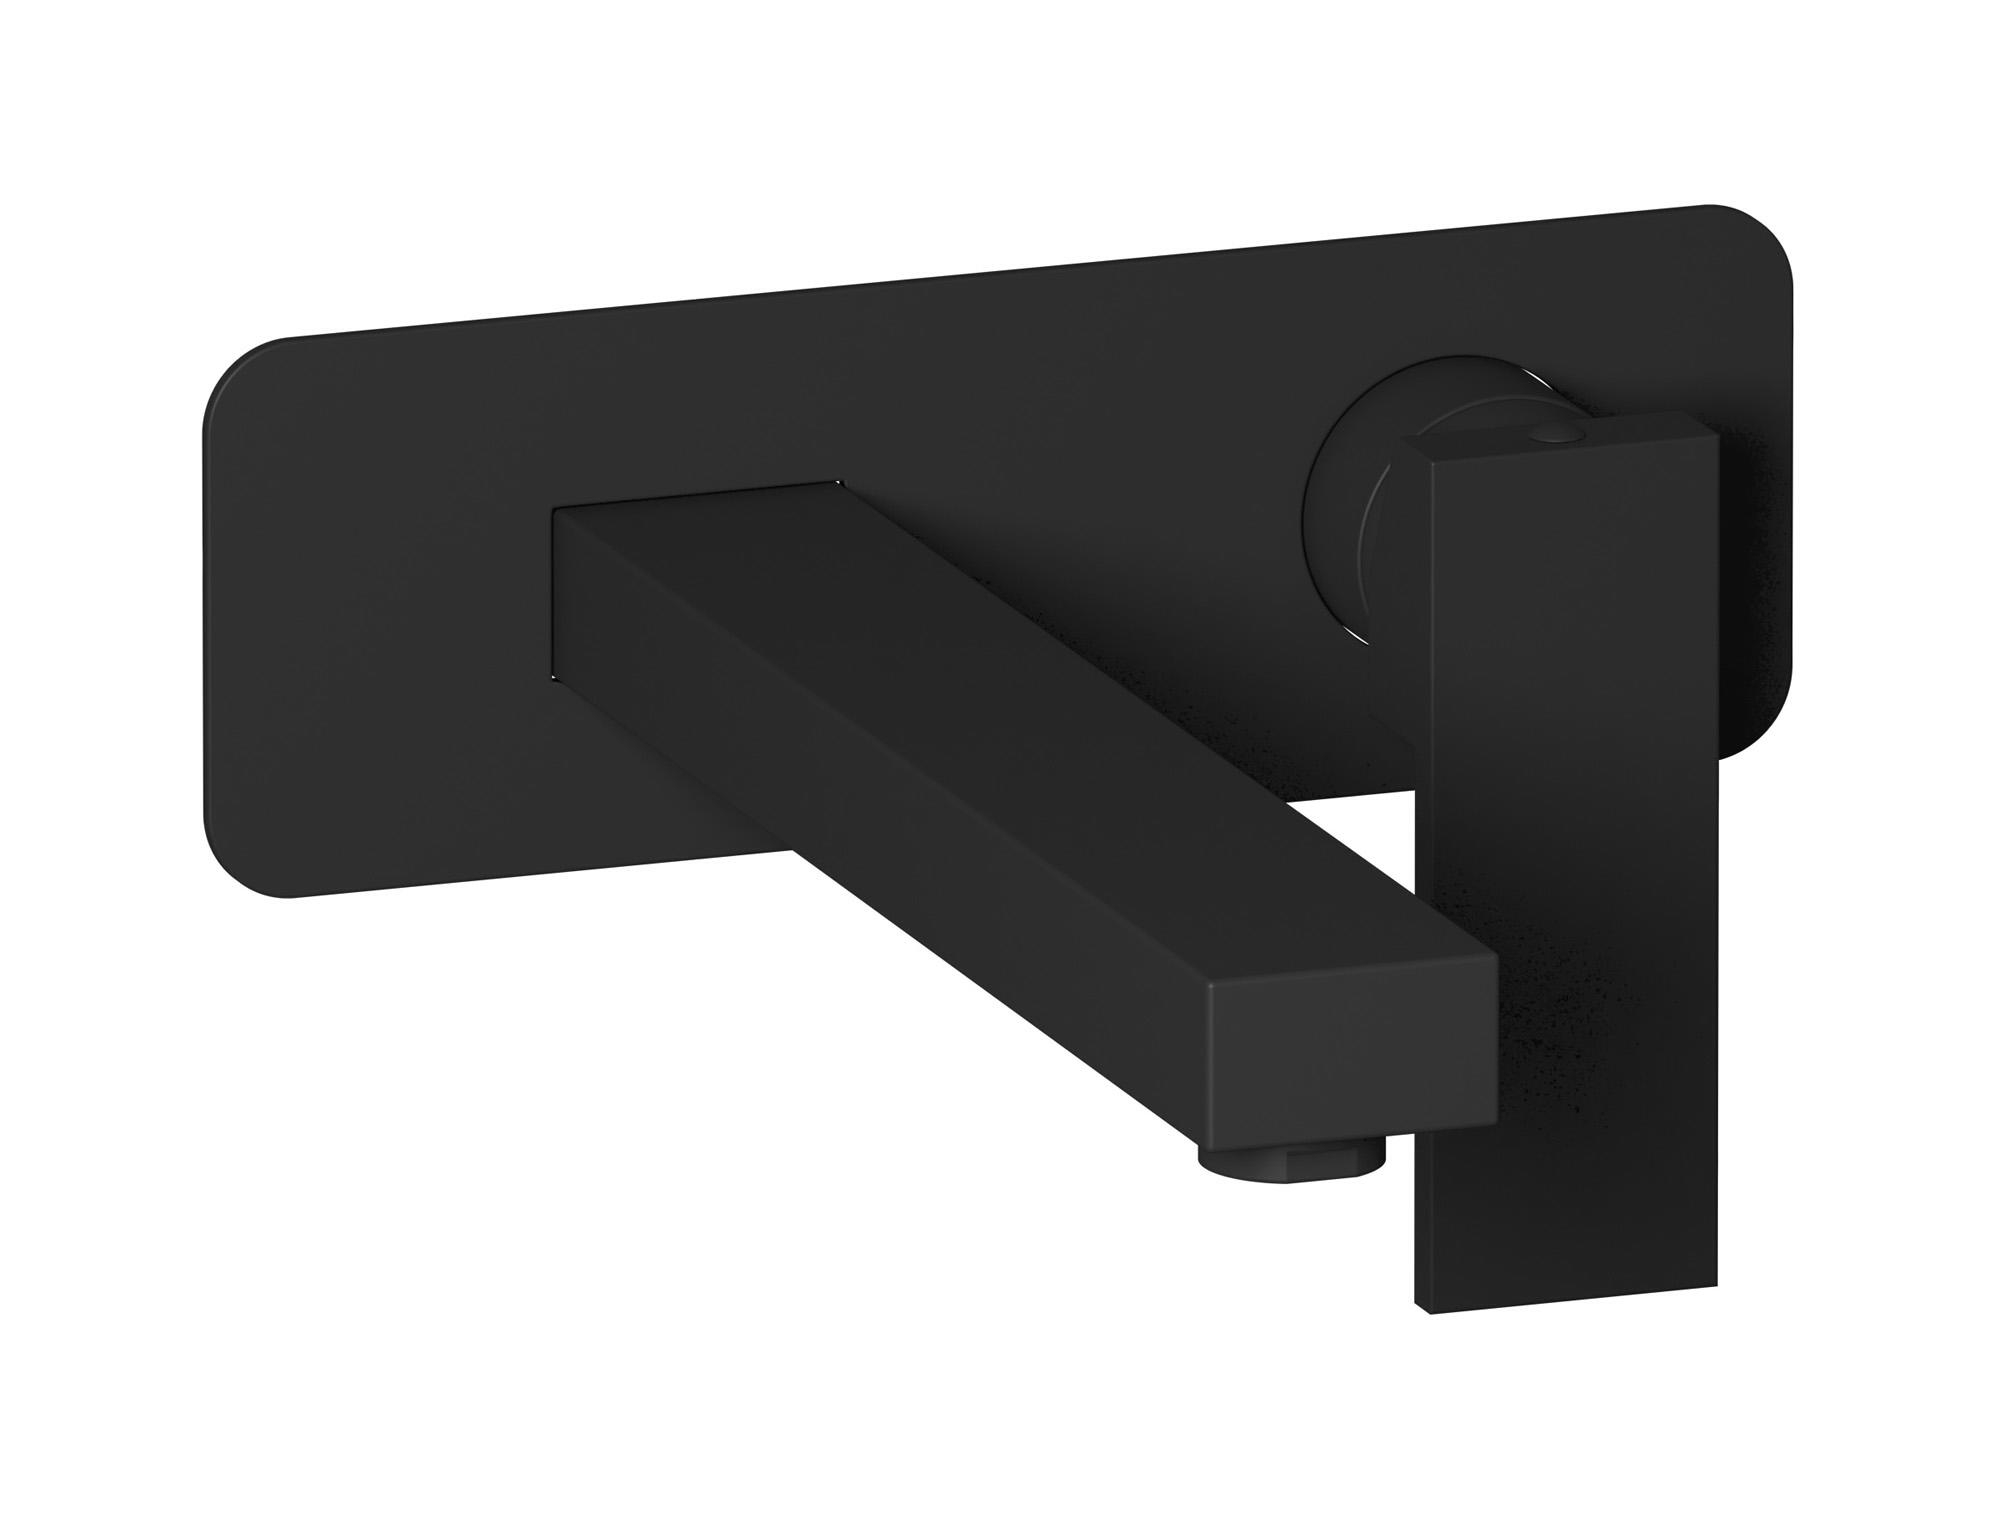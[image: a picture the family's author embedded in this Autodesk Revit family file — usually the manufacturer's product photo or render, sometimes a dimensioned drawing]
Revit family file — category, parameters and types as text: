
# Revit family: RU207
name_source: partatom
category: Apparecchi idraulici
units: mm (PartAtom-declared; Revit-internal decimal feet)

## family parameters
Basato su piano di lavoro = No
Condiviso = No
Mantieni orientamento annotazione = No
Numero OmniClass = 23.45.55.17
Punto di calcolo locali = No
Quota connettore circolare = Usa diametro
Sempre verticale = Sì
Taglio con vuoti quando caricato = No
Tipo di parte = Normale
Titolo OmniClass = Mixing Faucets

## types (12) — shared parameters
Cold water inlet = 10 mm  [stored 0.0328084 ft]
Commenti sul tipo = Wall mounted washbasin mixer with long spout complete with drain
Connessione CW = No
Connessione HW = No
Connessione di scarico = No
Connessione di ventilazione = No
Descrizione = Wall mounted washbasin mixer with long spout complete with drain
Hot water inlet = 10 mm  [stored 0.0328084 ft]
Produttore = IB Rubinetterie S.p.A.
URL = https://www.weareib.it
zero-valued in all types: Prospetto di default

## per-type parameters (varying)
| type | Finishes surface | Immagine tipo | Modello |
| Chrome | IB_Chrome | RU207CC.jpg | RU207CC |
| Matt White | IB_matt white | RU207BO.jpg | RU207BO |
| Black Chrome | IB_Black chrome | RU207CF.jpg | RU207CF |
| Brushed Black Chrome | IB_Brushed black chrome | RU207CS.jpg | RU207CS |
| Pale Gold | IB_Pale gold | RU207II.jpg | RU207II |
| Brushed Pale Gold | IB_brushed pale gold | RU207IS.jpg | RU207IS |
| Matt Black | IB_matt black | RU207NP.jpg | RU207NP |
| Gold | IB_gold | RU207OO.jpg | RU207OO |
| Brushed Gold | IB_brushed gold | RU207OS.jpg | RU207OS |
| Rose Gold | IB_Rose gold | RU207RS.jpg | RU207RS |
| Brushed Rose Gold | IB_Brushed rose gold | RU207SR.jpg | RU207SR |
| Brushed Nickel | IB_Brushed nickel | RU207SS.jpg | RU207SS |

note: [stored X ft] marks values corroborated as IEEE doubles in the binary element streams (Revit-internal decimal feet)
